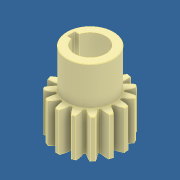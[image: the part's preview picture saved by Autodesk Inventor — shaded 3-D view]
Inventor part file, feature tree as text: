
AUTODESK INVENTOR PART (.ipt)
format: ipt  version: 2018 (Build 220112000, 112)  size: 381,952 bytes
history: native  units: mm
features: extrude x1, sketch x1, pattern_circular x1
ambient origin geometry x8: Origin, YZ Plane, XZ Plane, XY Plane, X Axis, Y Axis, Z Axis, Center Point
bodies: Solid1 (feature_tree)
feature tree (3):
  extrude  "Extrusion2"  Depth=2.0mm
  sketch  "Sketch2"  dims[d2=8.0mm d4=2.0mm d5=1.0mm d6=0.0mm d7=0.0mm d8=4.0mm d9=1.0mm]
  pattern_circular  "CirPattern1"
